# Revit family: LM0076101_Mueble Fussion Plus 80 Cm
name_source: partatom
category: Specialty Equipment
units: mm (PartAtom-declared; Revit-internal decimal feet)

## family parameters
Always vertical = Yes
Cut with Voids When Loaded = No
Part Type = Normal
Room Calculation Point = No
Round Connector Dimension = Use Diameter
Shared = No
Work Plane-Based = No

## types (1)
- LM0076101_Mueble Fussion Plus 80 Cm
    Alto = 450 mm  [stored 1.47638 ft]
    Altura Lavamanos = 100 mm  [stored 0.328084 ft]
    Ancho = 800 mm  [stored 2.62467 ft]
    Ancho Lavamanos = 802 mm  [stored 2.63123 ft]
    Canto = PVC rígido 22 mm de calibre.
    Creado por = IDD
    Densidad = 15mm 670 kg./m^3.
    Dimensiones generales del producto = 17,72” x 31,50” x 17,56” (450,0 x 800 x 446 mm).
    Fecha de creación = 30/07/2020
    Manufacturer = Corona
    Material = Corona_Porcelana_Sanitaria
    Material 2 = Corona_Madera_Aglomerada_Duna
    Material 3 = Corona_Madera_Aglomerada_Plomo
    Material 4 = Corona_Acero inoxidable
    Model = Mueble Fussion Plus 80 Cm
    Peso Bruto aprox = 34,2 lb (15,5 kg).
    Peso Neto aprox = 32 lb (14,5 kg).
    Profundida Lavamanos = 450 mm  [stored 1.47638 ft]
    Profundidad = 446 mm  [stored 1.46325 ft]
    Resistencia a la humedad = 8%.
    Resistencia al Rayado = 700 ciclos.

note: [stored X ft] marks values corroborated as IEEE doubles in the binary element streams (Revit-internal decimal feet)

## geometry (parser evidence)
native form markers: Sweep x2
no freeform markers — native parametric forms only
